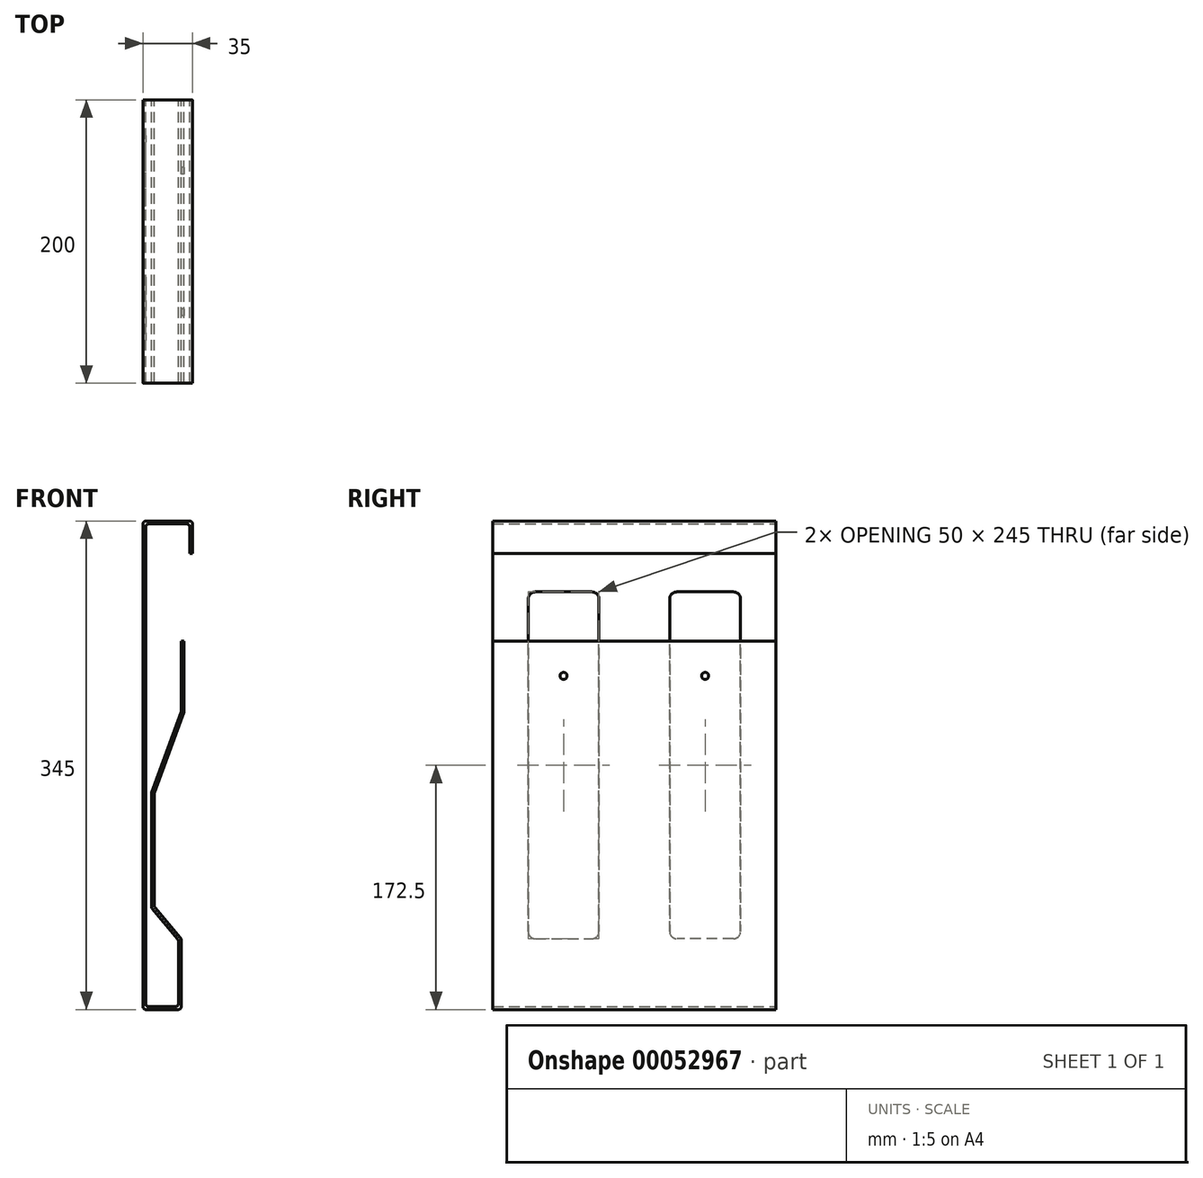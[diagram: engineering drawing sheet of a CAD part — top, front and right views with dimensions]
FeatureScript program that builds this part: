
annotation { "Feature Type Name" : "Feature", "Feature Type Description" : "" }
export const myFeature = defineFeature(function(context is Context, id is Id, definition is map)
    precondition{}
    {
        {
            var Q0;
            Q0=qCreatedBy(makeId("Front.planeOp"),FACE);
            var sketch = newSketch(context, id + "F0", { "sketchPlane" : qUnion([Q0])});
            skLineSegment(sketch, "E0", {"start": v(0, 0) * mm, "end": v(35, 0) * mm});
            skLineSegment(sketch, "E1", {"start": v(35, 0) * mm, "end": v(35, -23) * mm});
            skLineSegment(sketch, "E2", {"start": v(0, 0) * mm, "end": v(0, -345) * mm});
            skLineSegment(sketch, "E3", {"start": v(0, -345) * mm, "end": v(27, -345) * mm});
            skLineSegment(sketch, "E4", {"start": v(27, -295) * mm, "end": v(27, -345) * mm});
            skLineSegment(sketch, "E5.0", {"start": v(33, -2) * mm, "end": v(33, -23) * mm});
            skLineSegment(sketch, "E5.1", {"start": v(25, -295.73) * mm, "end": v(25, -343) * mm});
            skLineSegment(sketch, "E5.2", {"start": v(2, -343) * mm, "end": v(25, -343) * mm});
            skLineSegment(sketch, "E5.3", {"start": v(2, -2) * mm, "end": v(2, -343) * mm});
            skLineSegment(sketch, "E5.4", {"start": v(2, -2) * mm, "end": v(33, -2) * mm});
            skLineSegment(sketch, "E6", {"start": v(33, -23) * mm, "end": v(35, -23) * mm});
            skLineSegment(sketch, "E7", {"start": v(25, -295.73) * mm, "end": v(6, -273.08) * mm});
            skLineSegment(sketch, "E8", {"start": v(6, -273.08) * mm, "end": v(6, -192) * mm});
            skLineSegment(sketch, "E9", {"start": v(6, -192) * mm, "end": v(27, -134.3) * mm});
            skLineSegment(sketch, "E10", {"start": v(27, -134.3) * mm, "end": v(27, -84.66) * mm});
            skLineSegment(sketch, "E11.0", {"start": v(29, -134.66) * mm, "end": v(29, -84.66) * mm});
            skLineSegment(sketch, "E11.1", {"start": v(8, -192.36) * mm, "end": v(29, -134.66) * mm});
            skLineSegment(sketch, "E11.2", {"start": v(8, -272.36) * mm, "end": v(8, -192.36) * mm});
            skLineSegment(sketch, "E11.3", {"start": v(27, -295) * mm, "end": v(8, -272.36) * mm});
            skLineSegment(sketch, "E12", {"start": v(27, -84.66) * mm, "end": v(29, -84.66) * mm});
            skSolve(sketch);
        }
        {
            var Q0;
            Q0=qSketchRegion(id+"F0",true);
            extrude(context, id + "F1", {"entities" : qUnion([Q0]), "depth" : 200 * mm});
        }
        {
            var Q0;
            Q0=makeQuery(id+"F1.opExtrude","SWEPT_EDGE",EDGE,{"disambiguationData":[OSD([sQuery(id+"F0.wireOp",EDGE,"E0"),sQuery(id+"F0.wireOp",EDGE,"E2")])]});
            var Q1;
            Q1=makeQuery(id+"F1.opExtrude","SWEPT_EDGE",EDGE,{"disambiguationData":[OSD([sQuery(id+"F0.wireOp",EDGE,"E0"),sQuery(id+"F0.wireOp",EDGE,"E1")])]});
            var Q2;
            Q2=makeQuery(id+"F1.opExtrude","SWEPT_EDGE",EDGE,{"disambiguationData":[OSD([sQuery(id+"F0.wireOp",EDGE,"E5.0"),sQuery(id+"F0.wireOp",EDGE,"E5.4")])]});
            var Q3;
            Q3=makeQuery(id+"F1.opExtrude","SWEPT_EDGE",EDGE,{"disambiguationData":[OSD([sQuery(id+"F0.wireOp",EDGE,"E5.3"),sQuery(id+"F0.wireOp",EDGE,"E5.4")])]});
            var Q4;
            Q4=makeQuery(id+"F1.opExtrude","SWEPT_EDGE",EDGE,{"disambiguationData":[OSD([sQuery(id+"F0.wireOp",EDGE,"E2"),sQuery(id+"F0.wireOp",EDGE,"E3")])]});
            var Q5;
            Q5=makeQuery(id+"F1.opExtrude","SWEPT_EDGE",EDGE,{"disambiguationData":[OSD([sQuery(id+"F0.wireOp",EDGE,"E5.2"),sQuery(id+"F0.wireOp",EDGE,"E5.3")])]});
            var Q6;
            Q6=makeQuery(id+"F1.opExtrude","SWEPT_EDGE",EDGE,{"disambiguationData":[OSD([sQuery(id+"F0.wireOp",EDGE,"E3"),sQuery(id+"F0.wireOp",EDGE,"E4")])]});
            var Q7;
            Q7=makeQuery(id+"F1.opExtrude","SWEPT_EDGE",EDGE,{"disambiguationData":[OSD([sQuery(id+"F0.wireOp",EDGE,"E5.1"),sQuery(id+"F0.wireOp",EDGE,"E5.2")])]});
            var Q8;
            Q8=makeQuery(id+"F1.opExtrude","SWEPT_EDGE",EDGE,{"disambiguationData":[OSD([sQuery(id+"F0.wireOp",EDGE,"E5.1"),sQuery(id+"F0.wireOp",EDGE,"E7")])]});
            var Q9;
            Q9=makeQuery(id+"F1.opExtrude","SWEPT_EDGE",EDGE,{"disambiguationData":[OSD([sQuery(id+"F0.wireOp",EDGE,"E4"),sQuery(id+"F0.wireOp",EDGE,"E11.3")])]});
            var Q10;
            Q10=makeQuery(id+"F1.opExtrude","SWEPT_EDGE",EDGE,{"disambiguationData":[OSD([sQuery(id+"F0.wireOp",EDGE,"E11.2"),sQuery(id+"F0.wireOp",EDGE,"E11.3")])]});
            var Q11;
            Q11=makeQuery(id+"F1.opExtrude","SWEPT_EDGE",EDGE,{"disambiguationData":[OSD([sQuery(id+"F0.wireOp",EDGE,"E7"),sQuery(id+"F0.wireOp",EDGE,"E8")])]});
            var Q12;
            Q12=makeQuery(id+"F1.opExtrude","SWEPT_EDGE",EDGE,{"disambiguationData":[OSD([sQuery(id+"F0.wireOp",EDGE,"E8"),sQuery(id+"F0.wireOp",EDGE,"E9")])]});
            var Q13;
            Q13=makeQuery(id+"F1.opExtrude","SWEPT_EDGE",EDGE,{"disambiguationData":[OSD([sQuery(id+"F0.wireOp",EDGE,"E11.1"),sQuery(id+"F0.wireOp",EDGE,"E11.2")])]});
            var Q14;
            Q14=makeQuery(id+"F1.opExtrude","SWEPT_EDGE",EDGE,{"disambiguationData":[OSD([sQuery(id+"F0.wireOp",EDGE,"E11.0"),sQuery(id+"F0.wireOp",EDGE,"E11.1")])]});
            var Q15;
            Q15=makeQuery(id+"F1.opExtrude","SWEPT_EDGE",EDGE,{"disambiguationData":[OSD([sQuery(id+"F0.wireOp",EDGE,"E9"),sQuery(id+"F0.wireOp",EDGE,"E10")])]});
            fillet(context, id + "F2", {"entities" : qUnion([Q0, Q1, Q2, Q3, Q4, Q5, Q6, Q7, Q8, Q9, Q10, Q11, Q12, Q13, Q14, Q15]), "radius" : 2 * mm, "tangentPropagation" : true, "allowEdgeOverflow" : false});
        }
        {
            var Q0;
            Q0=makeQuery(id+"F1.opExtrude","SWEPT_FACE",FACE,{"disambiguationData":[OSD([sQuery(id+"F0.wireOp",EDGE,"E2")])]});
            var sketch = newSketch(context, id + "F3", { "sketchPlane" : qUnion([Q0])});
            skLineSegment(sketch, "E13", {"start": v(100, -2) * mm, "end": v(100, -58.7) * mm, "construction": true});
            skLineSegment(sketch, "E14.bottom", {"start": v(30, -50) * mm, "end": v(70, -50) * mm});
            skLineSegment(sketch, "E14.top", {"start": v(30, -295) * mm, "end": v(70, -295) * mm});
            skLineSegment(sketch, "E14.left", {"start": v(25, -55) * mm, "end": v(25, -290) * mm});
            skLineSegment(sketch, "E14.right", {"start": v(75, -55) * mm, "end": v(75, -290) * mm});
            skLineSegment(sketch, "E15.MirrorCS", {"start": v(125, -55) * mm, "end": v(125, -290) * mm});
            skLineSegment(sketch, "E16.MirrorCS", {"start": v(170, -50) * mm, "end": v(130, -50) * mm});
            skLineSegment(sketch, "E17.MirrorCS", {"start": v(175, -55) * mm, "end": v(175, -290) * mm});
            skLineSegment(sketch, "E18.MirrorCS", {"start": v(170, -295) * mm, "end": v(130, -295) * mm});
            skPoint(sketch, "E19.visualSharp", {"position": v(25, -50) * mm});
            skArc(sketch, "E19.filletArc", {"start": v(30, -50) * mm, "mid": v(26.46, -51.46) * mm, "end": v(25, -55) * mm});
            skPoint(sketch, "E20.visualSharp", {"position": v(75, -50) * mm});
            skArc(sketch, "E20.filletArc", {"start": v(75, -55) * mm, "mid": v(73.54, -51.46) * mm, "end": v(70, -50) * mm});
            skPoint(sketch, "E21.visualSharp", {"position": v(75, -295) * mm});
            skArc(sketch, "E21.filletArc", {"start": v(70, -295) * mm, "mid": v(73.54, -293.54) * mm, "end": v(75, -290) * mm});
            skPoint(sketch, "E22.visualSharp", {"position": v(25, -295) * mm});
            skArc(sketch, "E22.filletArc", {"start": v(25, -290) * mm, "mid": v(26.46, -293.54) * mm, "end": v(30, -295) * mm});
            skPoint(sketch, "E23.visualSharp", {"position": v(125, -50) * mm});
            skArc(sketch, "E23.filletArc", {"start": v(130, -50) * mm, "mid": v(126.46, -51.46) * mm, "end": v(125, -55) * mm});
            skPoint(sketch, "E24.visualSharp", {"position": v(175, -50) * mm});
            skArc(sketch, "E24.filletArc", {"start": v(175, -55) * mm, "mid": v(173.54, -51.46) * mm, "end": v(170, -50) * mm});
            skPoint(sketch, "E25.visualSharp", {"position": v(175, -295) * mm});
            skArc(sketch, "E25.filletArc", {"start": v(170, -295) * mm, "mid": v(173.54, -293.54) * mm, "end": v(175, -290) * mm});
            skPoint(sketch, "E26.visualSharp", {"position": v(125, -295) * mm});
            skArc(sketch, "E26.filletArc", {"start": v(125, -290) * mm, "mid": v(126.46, -293.54) * mm, "end": v(130, -295) * mm});
            skSolve(sketch);
        }
        {
            var Q0;
            Q0=makeQuery(id+"F3.imprint","IMPRINT",FACE,{"disambiguationData":[TD([[makeQuery(id+"F3.imprint","IMPRINT",EDGE,{"derivedFrom":sQuery(id+"F3.wireOp",EDGE,"E14.bottom")}),-1.0]])]});
            var Q1;
            Q1=makeQuery(id+"F3.imprint","IMPRINT",FACE,{"disambiguationData":[TD([[makeQuery(id+"F3.imprint","IMPRINT",EDGE,{"derivedFrom":sQuery(id+"F3.wireOp",EDGE,"E15.MirrorCS")}),1.0]])]});
            extrude(context, id + "F4", {"entities" : qUnion([Q0, Q1]), "operationType" : NewBodyOperationType.REMOVE, "oppositeDirection" : true, "depth" : 4 * mm});
        }
        {
            var Q0;
            Q0=makeQuery(id+"F1.opExtrude","SWEPT_FACE",FACE,{"disambiguationData":[OSD([sQuery(id+"F0.wireOp",EDGE,"E10")])]});
            var sketch = newSketch(context, id + "F5", { "sketchPlane" : qUnion([Q0])});
            skLineSegment(sketch, "E27", {"start": v(0, -109.3) * mm, "end": v(200, -109.3) * mm, "construction": true});
            skPoint(sketch, "E28", {"position": v(50, -109.3) * mm});
            skPoint(sketch, "E29", {"position": v(150, -109.3) * mm});
            skSolve(sketch);
        }
        {
            var Q0;
            Q0=sQuery(id+"F5.wireOp",VERTEX,"E28");
            var Q1;
            Q1=sQuery(id+"F5.wireOp",VERTEX,"E29");
            var Q2;
            Q2=makeQuery(id+"F1.opExtrude","SWEPT_BODY",BODY,{"disambiguationData":[OSD([sQuery(id+"F0.wireOp",EDGE,"E0"),sQuery(id+"F0.wireOp",EDGE,"E1"),sQuery(id+"F0.wireOp",EDGE,"E2"),sQuery(id+"F0.wireOp",EDGE,"E3"),sQuery(id+"F0.wireOp",EDGE,"E4"),sQuery(id+"F0.wireOp",EDGE,"E5.0"),sQuery(id+"F0.wireOp",EDGE,"E5.1"),sQuery(id+"F0.wireOp",EDGE,"E5.2"),sQuery(id+"F0.wireOp",EDGE,"E5.3"),sQuery(id+"F0.wireOp",EDGE,"E5.4"),sQuery(id+"F0.wireOp",EDGE,"E6"),sQuery(id+"F0.wireOp",EDGE,"E7"),sQuery(id+"F0.wireOp",EDGE,"E8"),sQuery(id+"F0.wireOp",EDGE,"E9"),sQuery(id+"F0.wireOp",EDGE,"E10"),sQuery(id+"F0.wireOp",EDGE,"E11.0"),sQuery(id+"F0.wireOp",EDGE,"E11.1"),sQuery(id+"F0.wireOp",EDGE,"E11.2"),sQuery(id+"F0.wireOp",EDGE,"E11.3"),sQuery(id+"F0.wireOp",EDGE,"E12")])]});
            hole(context, id + "F6", {"style" : HoleStyle.SIMPLE, "endStyle" : HoleEndStyle.BLIND, "holeDiameter" : 5 * mm, "holeDepth" : 2 * mm, "locations" : qUnion([Q0, Q1]), "scope" : qUnion([Q2])});
        }
    });
